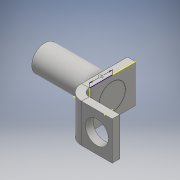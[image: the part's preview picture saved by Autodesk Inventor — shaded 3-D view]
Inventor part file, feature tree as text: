
AUTODESK INVENTOR PART (.ipt)
format: ipt  version: 2016 (Build 200138000, 138)  size: 167,424 bytes
history: native  units: mm
features: other x10, sketch x10, extrude x3
ambient origin geometry x8: Origin, YZ Plane, XZ Plane, XY Plane, X Axis, Y Axis, Z Axis, Center Point
bodies: Body1 (feature_tree)
feature tree (23):
  other  "Bryła1"
  other  "Powierzchnia1"
  sketch  "Szkic2"
  sketch  "Szkic3"
  other  "Kołnierz1"
  sketch  "Szkic5"
  sketch  "Szkic6"
  extrude  "Wyciągnięcie proste1"  Depth=5.0mm
  sketch  "Szkic7"
  other  "Powierzchnia2"
  extrude  "Wyciągnięcie proste2"  Depth=5.0mm
  extrude  "Wyciągnięcie proste3"  Depth=5.0mm
  sketch  "Szkic1"
  other  "Płyta1"
  sketch  "Szkic4"
  other  "Płyta2"
  other  "Gięcie1"
  other  "Narożnik1"
  sketch  "Szkic8"
  other  "Płyta3"
  other  "Gięcie2"
  sketch  "Szkic9"
  sketch  "Szkic10"
